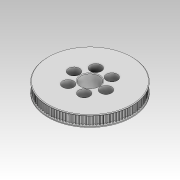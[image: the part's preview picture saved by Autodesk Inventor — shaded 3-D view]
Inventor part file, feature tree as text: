
AUTODESK INVENTOR PART (.ipt)
format: ipt  version: 2020 (Build 240168000, 168)  size: 1,133,056 bytes
history: native  units: mm
features: sketch x5, extrude x4, fillet x3, revolve x1, plane x1, pattern_circular x1, chamfer x1, projected_geometry x1
ambient origin geometry x8: Origin, YZ Plane, XZ Plane, XY Plane, X Axis, Y Axis, Z Axis, Center Point
bodies: Solid1 (feature_tree)
feature tree (17):
  revolve  "Revolution1"  [1 undecoded]
  extrude  "Extrusion1"  Depth=1.0mm
  plane  "Work Plane1"
  extrude  "Extrusion2"  Depth=33.425mm
  extrude  "Extrusion3"  TaperAngle=90.0deg  [1 undecoded]
  fillet  "Fillet1"  Radius=5.1mm
  pattern_circular  "Circular Pattern1"  Count=6 Angle=360.0deg
  fillet  "Fillet2"  [1 undecoded]
  chamfer  "Chamfer1"  [1 undecoded]
  fillet  "Fillet3"  Radius=9.0mm
  extrude  "Extrusion4"  Depth=7.0mm TaperAngle=0.0deg
  sketch  "Sketch1"  dims[d1=17.45mm d2=2.0mm]
  sketch  "Sketch2"  dims[d3=1.0mm d6=0.75mm]
  sketch  "Sketch3"  dims[d7=33.425mm d8=0.75mm]
  projected_geometry  "Projected Loop1"
  sketch  "Sketch4"  dims[d11=2.0mm d14=90.0deg d15=5.1mm]
  sketch  "Sketch5"  dims[d16=13.0mm d17=60.0mm d19=360.0deg d21=0.0mm d22=0.0mm d23=-5.0mm d24=9.0mm d25=7.0mm d26=0.0mm d27=7.5mm d29=1.0mm d30=66.85mm d31=10.0mm d32=0.0mm d33=1050.0mm d34=360.0deg d36=3.0mm d37=0.7mm d38=7.0mm d39=11.34464mm d41=34.125mm d42=0.6mm d43=0.75mm d44=0.4mm d45=0.5mm d46=0.5mm d47=2.0mm d48=45.0deg d49=1.0mm d50=0.2mm d51=0.0mm]
note: 4 required parameter values undecoded (feature->parameter linkage not recoverable at this tier; creation-order binding heuristic only, values carry confidence <= 0.55)